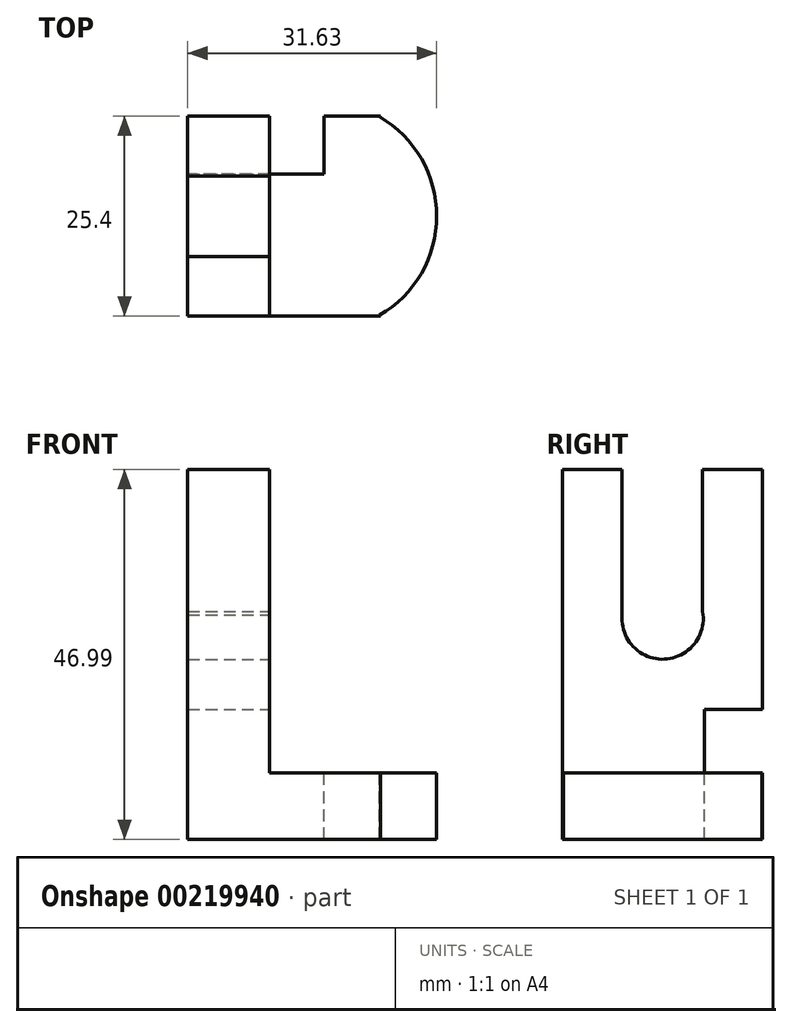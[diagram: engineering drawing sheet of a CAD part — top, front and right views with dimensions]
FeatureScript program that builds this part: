
annotation { "Feature Type Name" : "Feature", "Feature Type Description" : "" }
export const myFeature = defineFeature(function(context is Context, id is Id, definition is map)
    precondition{}
    {
        {
            var Q0;
            Q0=qCreatedBy(makeId("Front.planeOp"),FACE);
            var sketch = newSketch(context, id + "F0", { "sketchPlane" : qUnion([Q0])});
            skLineSegment(sketch, "E0", {"start": v(31.63, 0) * mm, "end": v(0, 0) * mm});
            skLineSegment(sketch, "E1", {"start": v(0, 0) * mm, "end": v(0, 47) * mm});
            skLineSegment(sketch, "E2", {"start": v(0, 47) * mm, "end": v(10.4, 47) * mm});
            skLineSegment(sketch, "E3", {"start": v(10.4, 47) * mm, "end": v(10.4, 8.43) * mm});
            skLineSegment(sketch, "E4", {"start": v(10.4, 8.43) * mm, "end": v(31.63, 8.43) * mm});
            skLineSegment(sketch, "E5", {"start": v(31.63, 8.43) * mm, "end": v(31.63, 0) * mm});
            skSolve(sketch);
        }
        {
            var Q0;
            Q0 = qSketchRegion(id + "F0", true);
            extrude(context, id + "F1", {"entities" : qUnion([Q0]), "depth" : 25.4 * mm});
        }
        {
            var Q0;
            Q0=makeQuery(id+"F1.opExtrude","SWEPT_FACE",FACE,{"disambiguationData":[OSD([sQuery(id+"F0.wireOp",EDGE,"E4")])]});
            var sketch = newSketch(context, id + "F2", { "sketchPlane" : qUnion([Q0])});
            skArc(sketch, "E6", {"start": v(24.35, -25.3) * mm, "mid": v(31.63, -12.7) * mm, "end": v(24.35, -0.1) * mm});
            skPoint(sketch, "E7.center.orphan", {"position": v(31.63, -12.7) * mm});
            skArc(sketch, "E8", {"start": v(24.35, -25.3) * mm, "mid": v(46.2, -12.7) * mm, "end": v(24.35, -0.1) * mm});
            skSolve(sketch);
        }
        {
            var Q0;
            Q0 = qSketchRegion(id + "F2", true);
            extrude(context, id + "F3", {"entities" : qUnion([Q0]), "operationType" : NewBodyOperationType.REMOVE, "oppositeDirection" : true, "depth" : 25.4 * mm});
        }
        {
            var Q0;
            Q0=makeQuery(id+"F1.opExtrude","SWEPT_FACE",FACE,{"disambiguationData":[OSD([sQuery(id+"F0.wireOp",EDGE,"E3")])]});
            var sketch = newSketch(context, id + "F4", { "sketchPlane" : qUnion([Q0])});
            skArc(sketch, "E9", {"start": v(-17.85, 28.5) * mm, "mid": v(-12.48, 22.9) * mm, "end": v(-7.6, 28.93) * mm});
            skLineSegment(sketch, "E10", {"start": v(-17.85, 27.62) * mm, "end": v(-17.85, 47) * mm});
            skLineSegment(sketch, "E11", {"start": v(-7.6, 27.18) * mm, "end": v(-7.6, 47) * mm});
            skLineSegment(sketch, "E12", {"start": v(-7.6, 47) * mm, "end": v(-17.85, 47) * mm});
            skPoint(sketch, "E13.orphan", {"position": v(-12.7, 47) * mm});
            skSolve(sketch);
        }
        {
            var Q0;
            Q0 = qSketchRegion(id + "F4", true);
            extrude(context, id + "F5", {"entities" : qUnion([Q0]), "operationType" : NewBodyOperationType.REMOVE, "oppositeDirection" : true, "depth" : 25.4 * mm});
        }
        {
            var Q0;
            Q0=makeQuery(id+"F1.opExtrude","CAP_FACE",FACE,{"disambiguationData":[OSD([sQuery(id+"F0.wireOp",EDGE,"E0"),sQuery(id+"F0.wireOp",EDGE,"E1"),sQuery(id+"F0.wireOp",EDGE,"E2"),sQuery(id+"F0.wireOp",EDGE,"E3"),sQuery(id+"F0.wireOp",EDGE,"E4"),sQuery(id+"F0.wireOp",EDGE,"E5")])],"isStart":true});
            var sketch = newSketch(context, id + "F6", { "sketchPlane" : qUnion([Q0])});
            skLineSegment(sketch, "E14.bottom", {"start": v(0, 0) * mm, "end": v(-17.32, 0) * mm});
            skLineSegment(sketch, "E14.top", {"start": v(0, 16.51) * mm, "end": v(-17.32, 16.51) * mm});
            skLineSegment(sketch, "E14.left", {"start": v(0, 0) * mm, "end": v(0, 16.51) * mm});
            skLineSegment(sketch, "E14.right", {"start": v(-17.32, 0) * mm, "end": v(-17.32, 16.51) * mm});
            skSolve(sketch);
        }
        {
            var Q0;
            Q0 = qSketchRegion(id + "F6", true);
            extrude(context, id + "F7", {"entities" : qUnion([Q0]), "operationType" : NewBodyOperationType.REMOVE, "oppositeDirection" : true, "depth" : 7.37 * mm});
        }
    });
